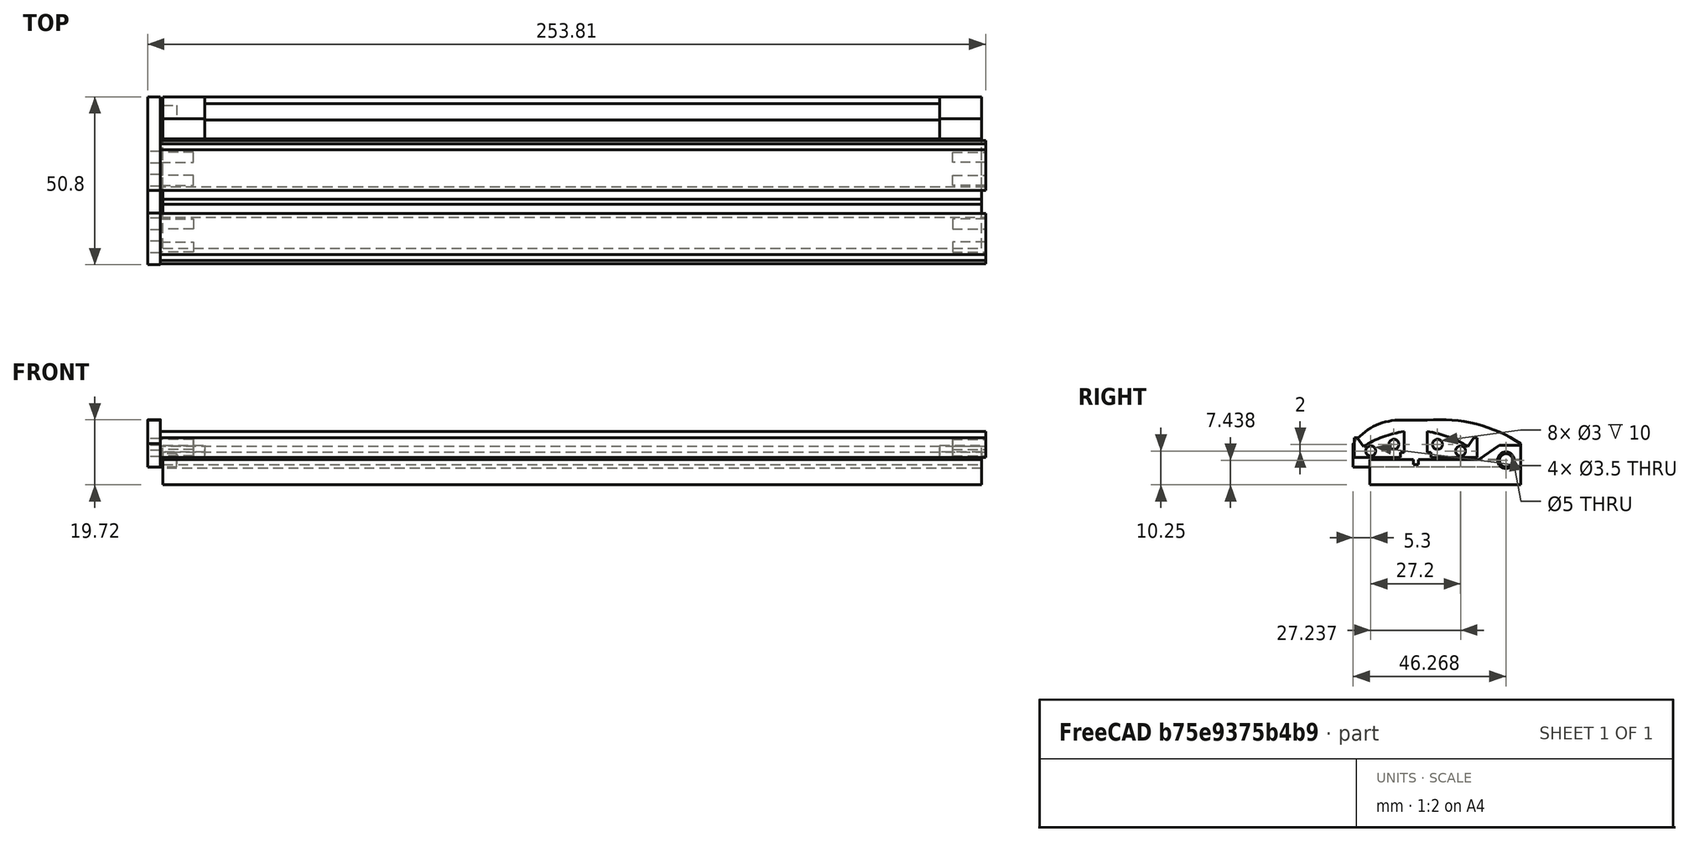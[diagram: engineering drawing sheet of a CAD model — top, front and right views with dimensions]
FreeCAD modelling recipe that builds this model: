
FCSTD DOCUMENT  (FreeCAD 0.19R24291 (Git))
Label: paper_cutter
License: All rights reserved
LicenseURL: http://en.wikipedia.org/wiki/All_rights_reserved
objects: App::FeaturePython×6, Part::FeaturePython×4, Part::Cylinder×4, Part::Cut×4
note: 12 computed .brp shape members not serialized (recipe doc carries the construction recipe); baked Part::Feature solids carry a one-line shape summary decoded from their .brp

FEATURE [Part::FeaturePython] b_rail_001_  label="rail_001"  # a2plus imported part (geometry in sourceFile) (typed FeaturePython)
  Placement = pos=(0,0.3,0) rot=(0,0,1;0rad)
  a2p_Version = V0.1
  fixedPosition = true
  muxInfo = [VERTEXES] | V;Pad;1;16; | V;Pad;2;16; | V;Pad;3;16; | V;Pad;4;16; | V;Pad;15;16; | V;Pad;16;16; | V;Pad;5;16; | V;Pad;6;16; | V;Pad;13;16; | V;Pad;7;16; | V;Pad;11;16; | V;Pad;9;16; | V;Pocket001;1;4; | V;Pocket001;2;4; | V;Pad;14;16; | V;Pad;8;16; | V;Pad;12;16; | V;Pad;10;16; | V;Pocket;1;4; | V;Pocket;2;4; | V;Pocket001;3;4; | V;Pocket001;4;4; | V;Pocket;3;4; | V;Pocket;4;4; | [EDGES] | E;Pad;1;24; | E;Pad;2;24; | E;Pad;3;24; | E;Pad;4;24; | E;Pad;20;24; | E;Pad;23;24; | E;Pad;24;24; | E;Pad;5;24; | E;Pad;6;24; | E;Pad;7;24; | E;Pad;21;24; | E;Pad;9;24; | E;Pad;18;24; | E;Pad;12;24; | E;Pad;15;24; | E;Pocket001;1;6; | E;Pocket001;2;6; | E;Pad;22;24; | E;Pad;10;24; | E;Pad;19;24; | E;Pad;13;24; | E;Pad;16;24; | E;Pocket;1;6; | E;Pocket;2;6; | E;Pad;17;24; | E;Pad;8;24; | E;Pad;14;24; | E;Pad;11;24; | E;Pocket001;3;6; | E;Pocket001;4;6; | E;Pocket001;5;6; | E;Pocket001;6;6; | E;Pocket;3;6; | E;Pocket;4;6; | E;Pocket;5;6; | E;Pocket;6;6; | [FACES] | F;Pad;1;10; | F;Pad;8;10; | F;Pad;2;10; | F;Pad;9;10; | F;Pad;10;10; | F;Pad;7;10; | F;Pad;3;10; | F;Pad;6;10; | F;Pad;4;10; | F;Pad;5;10; | F;Pocket001;1;18; | F;Pocket001;2;18; | F;Pocket;1;14; | F;Pocket;2;14; | F;Pocket001;3;18; | F;Pocket001;4;18; | F;Pocket;3;14; | F;Pocket;4;14;
  objectType = a2pPart
  sourceFile = .\rail.FCStd
  subassemblyImport = false
  timeLastImport = 1.64038e+09
  updateColors = true
FEATURE [Part::FeaturePython] b_rail_001_001  label="rail_002"  # a2plus imported part (geometry in sourceFile) (typed FeaturePython)
  Placement = pos=(250,37.5369,1.444e-13) rot=(0,0,1;3.14159rad)
  a2p_Version = V0.1
  fixedPosition = false
  muxInfo = [VERTEXES] | V;Pad;1;16; | V;Pad;2;16; | V;Pad;3;16; | V;Pad;4;16; | V;Pad;15;16; | V;Pad;16;16; | V;Pad;5;16; | V;Pad;6;16; | V;Pad;13;16; | V;Pad;7;16; | V;Pad;11;16; | V;Pad;9;16; | V;Pocket001;1;4; | V;Pocket001;2;4; | V;Pad;14;16; | V;Pad;8;16; | V;Pad;12;16; | V;Pad;10;16; | V;Pocket;1;4; | V;Pocket;2;4; | V;Pocket001;3;4; | V;Pocket001;4;4; | V;Pocket;3;4; | V;Pocket;4;4; | [EDGES] | E;Pad;1;24; | E;Pad;2;24; | E;Pad;3;24; | E;Pad;4;24; | E;Pad;20;24; | E;Pad;23;24; | E;Pad;24;24; | E;Pad;5;24; | E;Pad;6;24; | E;Pad;7;24; | E;Pad;21;24; | E;Pad;9;24; | E;Pad;18;24; | E;Pad;12;24; | E;Pad;15;24; | E;Pocket001;1;6; | E;Pocket001;2;6; | E;Pad;22;24; | E;Pad;10;24; | E;Pad;19;24; | E;Pad;13;24; | E;Pad;16;24; | E;Pocket;1;6; | E;Pocket;2;6; | E;Pad;17;24; | E;Pad;8;24; | E;Pad;14;24; | E;Pad;11;24; | E;Pocket001;3;6; | E;Pocket001;4;6; | E;Pocket001;5;6; | E;Pocket001;6;6; | E;Pocket;3;6; | E;Pocket;4;6; | E;Pocket;5;6; | E;Pocket;6;6; | [FACES] | F;Pad;1;10; | F;Pad;8;10; | F;Pad;2;10; | F;Pad;9;10; | F;Pad;10;10; | F;Pad;7;10; | F;Pad;3;10; | F;Pad;6;10; | F;Pad;4;10; | F;Pad;5;10; | F;Pocket001;1;18; | F;Pocket001;2;18; | F;Pocket;1;14; | F;Pocket;2;14; | F;Pocket001;3;18; | F;Pocket001;4;18; | F;Pocket;3;14; | F;Pocket;4;14;
  objectType = a2pPart
  sourceFile = .\rail.FCStd
  subassemblyImport = false
  timeLastImport = 1.64038e+09
  updateColors = true
FEATURE [App::FeaturePython] planeCoincident_001  label="planeCoincident_001__rail_001"  # a2plus constraint (typed FeaturePython)
  Object1 = b_rail_001_001
  Object2 = b_rail_001_
  ParentTreeObject = -> b_rail_001_001
  SubElement1 = Face4
  SubElement2 = Face5
  Suppressed = false
  Type = plane
  directionConstraint = 1
  offset = 0
FEATURE [App::FeaturePython] planeCoincident_001_mirror  label="planeCoincident_001__rail_002"  # a2plus constraint (typed FeaturePython)
  Object1 = b_rail_001_001
  Object2 = b_rail_001_
  ParentTreeObject = -> b_rail_001_
  SubElement1 = Face4
  SubElement2 = Face5
  Suppressed = false
  Type = plane
  directionConstraint = 1
  offset = 0
FEATURE [App::FeaturePython] planeCoincident_002  label="planeCoincident_002__rail_001"  # a2plus constraint (typed FeaturePython)
  Object1 = b_rail_001_001
  Object2 = b_rail_001_
  ParentTreeObject = -> b_rail_001_001
  SubElement1 = Face1
  SubElement2 = Face1
  Suppressed = false
  Type = plane
  directionConstraint = 0
  offset = 0
FEATURE [App::FeaturePython] planeCoincident_002_mirror  label="planeCoincident_002__rail_002"  # a2plus constraint (typed FeaturePython)
  Object1 = b_rail_001_001
  Object2 = b_rail_001_
  ParentTreeObject = -> b_rail_001_
  SubElement1 = Face1
  SubElement2 = Face1
  Suppressed = false
  Type = plane
  directionConstraint = 0
  offset = 0
FEATURE [Part::FeaturePython] b_cutter_endv2_001_  label="cutter_endv2_001"  # a2plus imported part (geometry in sourceFile) (typed FeaturePython)
  Placement = pos=(-3.81,0.00358582,-2.94371) rot=(0,0,1;0rad)
  a2p_Version = V0.1
  fixedPosition = false
  muxInfo = [VERTEXES] | V;Pad;1;12; | V;Pad;2;12; | V;Pad;3;12; | V;Pad;4;12; | V;Pad;11;12; | V;Pad;12;12; | V;Pad;5;12; | V;Pad;6;12; | V;Pad;7;12; | V;Pad;9;12; | V;Pad;10;12; | V;Pad;8;12; | V;Pad001;1;2; | V;Pad001;2;2; | [EDGES] | E;Pad;1;18; | E;Pad;2;18; | E;Pad;3;18; | E;Pad;4;18; | E;Pad;14;18; | E;Pad;17;18; | E;Pad;18;18; | E;Pad;5;18; | E;Pad;6;18; | E;Pad;7;18; | E;Pad;9;18; | E;Pad;12;18; | E;Pad;15;18; | E;Pad;16;18; | E;Pad;10;18; | E;Pad;13;18; | E;Pad001;1;3; | E;Pad;11;18; | E;Pad;8;18; | E;Pad001;2;3; | E;Pad001;3;3; | [FACES] | F;Pad;1;8; | F;Pad;6;8; | F;Pad;2;8; | F;Pad;7;8; | F;Pad;8;8; | F;Pad;5;8; | F;Pad;3;8; | F;Pad;4;8; | F;Pad001;1;10; | F;Pad001;2;10;
  objectType = a2pPart
  sourceFile = .\cutter_endv2.FCStd
  subassemblyImport = false
  timeLastImport = 1.64038e+09
  updateColors = true
FEATURE [App::FeaturePython] planeCoincident_003  label="planeCoincident_003__rail_001"  # a2plus constraint (typed FeaturePython)
  Object1 = b_cutter_endv2_001_
  Object2 = b_rail_001_
  ParentTreeObject = -> b_cutter_endv2_001_
  SubElement1 = Face5
  SubElement2 = Face4
  Suppressed = false
  Type = plane
  directionConstraint = 1
  offset = 0
FEATURE [App::FeaturePython] planeCoincident_003_mirror  label="planeCoincident_003__cutter_endv2_001"  # a2plus constraint (typed FeaturePython)
  Object1 = b_cutter_endv2_001_
  Object2 = b_rail_001_
  ParentTreeObject = -> b_rail_001_
  SubElement1 = Face5
  SubElement2 = Face4
  Suppressed = false
  Type = plane
  directionConstraint = 1
  offset = 0
FEATURE [Part::FeaturePython] b_hinge_001_  label="hinge_001"  # a2plus imported part (geometry in sourceFile) (typed FeaturePython)
  Placement = pos=(0.806136,4.96832,-8.24974) rot=(0,0,1;0rad)
  a2p_Version = V0.1
  fixedPosition = false
  muxInfo = [VERTEXES] | V;Pad;1;24; | V;Pad;2;24; | V;Pad;3;24; | V;Pad;4;24; | V;Pad;21;24; | V;Pad;22;24; | V;Pad;5;24; | V;Pad;6;24; | V;Pad;7;24; | V;Pad;9;24; | V;Pad;11;24; | V;Pad;13;24; | V;Pad;15;24; | V;Pad;17;24; | V;Pad;19;24; | V;Pad;23;24; | V;Pad;8;24; | V;Pad;10;24; | V;Pad;12;24; | V;Pad;14;24; | V;Pad;16;24; | V;Pad;18;24; | V;Pad;20;24; | V;Pad;24;24; | V;Pocket;1;12; | V;Pocket;2;12; | V;Pocket;3;12; | V;Pocket;4;12; | V;Pocket;5;12; | V;Pocket;6;12; | V;Pocket;7;12; | V;Pocket;8;12; | V;Pocket;9;12; | V;Pocket;10;12; | V;Pocket;11;12; | V;Pocket;12;12; | [EDGES] | E;Pad;1;36; | E;Pad;2;36; | E;Pad;3;36; | E;Pad;4;36; | E;Pad;29;36; | E;Pad;32;36; | E;Pad;33;36; | E;Pad;5;36; | E;Pad;6;36; | E;Pad;7;36; | E;Pad;9;36; | E;Pad;12;36; | E;Pad;15;36; | E;Pad;18;36; | E;Pad;21;36; | E;Pad;24;36; | E;Pad;27;36; | E;Pad;30;36; | E;Pad;35;36; | E;Pad;10;36; | E;Pad;13;36; | E;Pad;16;36; | E;Pad;19;36; | E;Pad;22;36; | E;Pad;25;36; | E;Pad;28;36; | E;Pad;31;36; | E;Pad;36;36; | E;Pad;26;36; | E;Pad;8;36; | E;Pocket;1;18; | E;Pocket;2;18; | E;Pocket;3;18; | E;Pad;8;36; | E;Pad;11;36; | E;Pocket;4;18; | E;Pocket;5;18; | E;Pocket;6;18; | E;Pocket;7;18; | E;Pad;11;36; | E;Pad;14;36; | E;Pad;17;36; | E;Pad;20;36; | E;Pad;23;36; | E;Pad;34;36; | E;Pocket;8;18; | E;Pocket;9;18; | E;Pocket;10;18; | E;Pocket;11;18; | E;Pocket;12;18; | E;Pocket;13;18; | E;Pocket;14;18; | E;Pocket;15;18; | E;Pocket;16;18; | [FACES] | F;Pad;1;14; | F;Pad;10;14; | F;Pad;2;14; | F;Pad;12;14; | F;Pad;13;14; | F;Pad;9;14; | F;Pad;2;14; | F;Pad;3;14; | F;Pad;4;14; | F;Pad;5;14; | F;Pad;6;14; | F;Pad;7;14; | F;Pad;8;14; | F;Pad;11;14; | F;Pad;3;14; | F;Pocket;1;19; | F;Pocket;2;19; | F;Pocket;3;19; | F;Pocket;4;19;
  objectType = a2pPart
  sourceFile = .\hinge.FCStd
  subassemblyImport = false
  timeLastImport = 1.64038e+09
  updateColors = true
FEATURE [Part::Cylinder] Cylinder
  Angle = 360
  AttacherType = Attacher::AttachEngine3D
  Height = 10
  Placement = pos=(3,12.3,4) rot=(0,-1,0;1.5708rad)
  Radius = 1.75
FEATURE [Part::Cylinder] Cylinder001
  Angle = 360
  AttacherType = Attacher::AttachEngine3D
  Height = 10
  Placement = pos=(3,25.5,4) rot=(0,-1,0;1.5708rad)
  Radius = 1.75
FEATURE [Part::Cylinder] Cylinder002
  Angle = 360
  AttacherType = Attacher::AttachEngine3D
  Height = 10
  Placement = pos=(3,32.5,2) rot=(0,-1,0;1.5708rad)
  Radius = 1.75
FEATURE [Part::Cylinder] Cylinder003
  Angle = 360
  AttacherType = Attacher::AttachEngine3D
  Height = 10
  Placement = pos=(3,5.3,2) rot=(0,-1,0;1.5708rad)
  Radius = 1.75
FEATURE [Part::Cut] Cut
  Base = -> b_cutter_endv2_001_
  Tool = -> Cylinder003
FEATURE [Part::Cut] Cut001
  Base = -> Cut
  Tool = -> Cylinder
FEATURE [Part::Cut] Cut002
  Base = -> Cut001
  Tool = -> Cylinder001
FEATURE [Part::Cut] Cut003
  Base = -> Cut002
  Tool = -> Cylinder002
